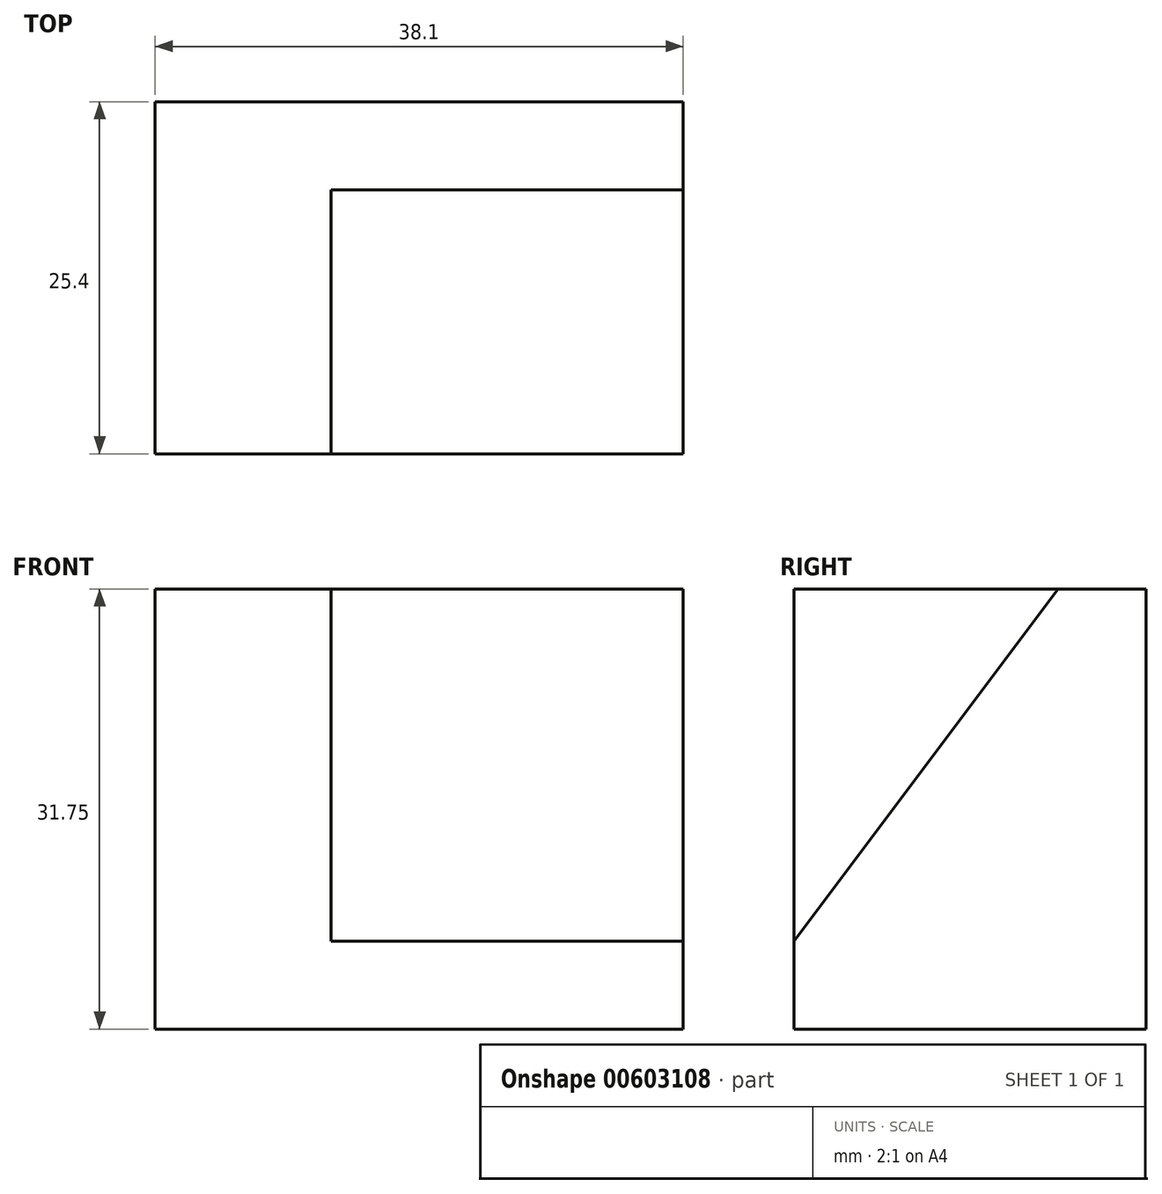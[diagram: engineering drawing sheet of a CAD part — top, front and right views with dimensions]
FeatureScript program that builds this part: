
annotation { "Feature Type Name" : "Feature", "Feature Type Description" : "" }
export const myFeature = defineFeature(function(context is Context, id is Id, definition is map)
    precondition{}
    {
        {
            var Q0;
            Q0=qCreatedBy(makeId("Front.planeOp"),FACE);
            var sketch = newSketch(context, id + "F0", { "sketchPlane" : qUnion([Q0])});
            skLineSegment(sketch, "E0", {"start": v(0, 0) * mm, "end": v(38.1, 0) * mm});
            skLineSegment(sketch, "E1", {"start": v(38.1, 0) * mm, "end": v(38.1, 31.75) * mm});
            skLineSegment(sketch, "E2", {"start": v(38.1, 31.75) * mm, "end": v(0, 31.75) * mm});
            skLineSegment(sketch, "E3", {"start": v(0, 31.75) * mm, "end": v(0, 0) * mm});
            skSolve(sketch);
        }
        {
            var Q0;
            Q0=makeQuery(id+"F0.imprint","IMPRINT",FACE,{"disambiguationData":[TD([[makeQuery(id+"F0.imprint","IMPRINT",EDGE,{"derivedFrom":sQuery(id+"F0.wireOp",EDGE,"E0")}),1.0]])]});
            extrude(context, id + "F1", {"entities" : qUnion([Q0]), "depth" : 25.4 * mm, "offsetDistance" : 25.4 * mm});
        }
        {
            var Q0;
            Q0=makeQuery(id+"F1.opExtrude","SWEPT_FACE",FACE,{"disambiguationData":[OSD([sQuery(id+"F0.wireOp",EDGE,"E1")])]});
            var sketch = newSketch(context, id + "F2", { "sketchPlane" : qUnion([Q0])});
            skLineSegment(sketch, "E4", {"start": v(0, 0) * mm, "end": v(0, 31.75) * mm});
            skLineSegment(sketch, "E5", {"start": v(0, 31.75) * mm, "end": v(-6.35, 31.75) * mm});
            skLineSegment(sketch, "E6", {"start": v(0, 0) * mm, "end": v(-25.4, 0) * mm});
            skLineSegment(sketch, "E7", {"start": v(-25.4, 0) * mm, "end": v(-25.4, 6.35) * mm});
            skLineSegment(sketch, "E8", {"start": v(-25.4, 6.35) * mm, "end": v(-25.4, 31.75) * mm});
            skLineSegment(sketch, "E9", {"start": v(-25.4, 31.75) * mm, "end": v(-6.35, 31.75) * mm});
            skLineSegment(sketch, "E10", {"start": v(-25.4, 6.35) * mm, "end": v(-6.35, 31.75) * mm});
            skSolve(sketch);
        }
        {
            var Q0;
            Q0=makeQuery(id+"F2.imprint","IMPRINT",FACE,{"disambiguationData":[TD([[makeQuery(id+"F2.imprint","IMPRINT",EDGE,{"derivedFrom":sQuery(id+"F2.wireOp",EDGE,"E8")}),-1.0]])]});
            extrude(context, id + "F3", {"entities" : qUnion([Q0]), "operationType" : NewBodyOperationType.REMOVE, "oppositeDirection" : true, "depth" : 25.4 * mm, "offsetDistance" : 25.4 * mm});
        }
    });
